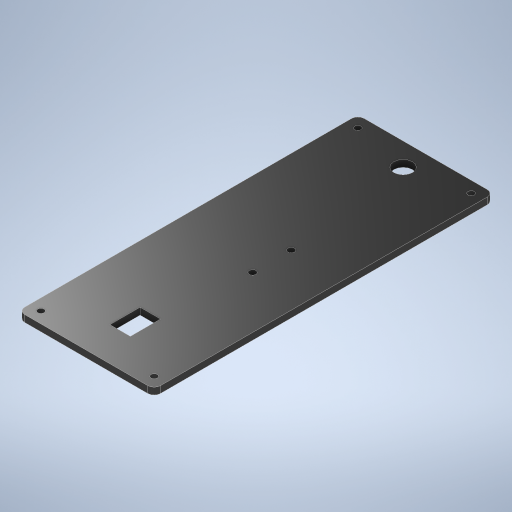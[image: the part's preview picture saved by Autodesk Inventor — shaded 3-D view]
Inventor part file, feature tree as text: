
AUTODESK INVENTOR PART (.ipt)
format: ipt  version: 2023 (Build 270158000, 158)  size: 275,968 bytes
history: native  units: in
note: dims shown in document units (in); Inventor stores cm internally (conversion verified against a paired STEP export)
features: other x3, extrude x2, sketch x1
ambient origin geometry x8: Origin, YZ Plane, XZ Plane, XY Plane, X Axis, Y Axis, Z Axis, Center Point
bodies: Solid1 (feature_tree)
feature tree (6):
  other  "MatTren.ipt"
  extrude  "Extrusion1"  Depth=0.3937in
  extrude  "Extrusion2"  Depth=0.5906in
  other  "Solid1::MatTren.ipt"
  other  "TaggingFeature1"
  sketch  "Sketch1"  dims[d0=0.3937in d1=0.1772in d2=0.5906in d3=0.1772in d4=0.5236in d5=0.3937in d6=0.0in d7=0.3937in d8=0.3268in d9=0.3937in d10=0.0in]
